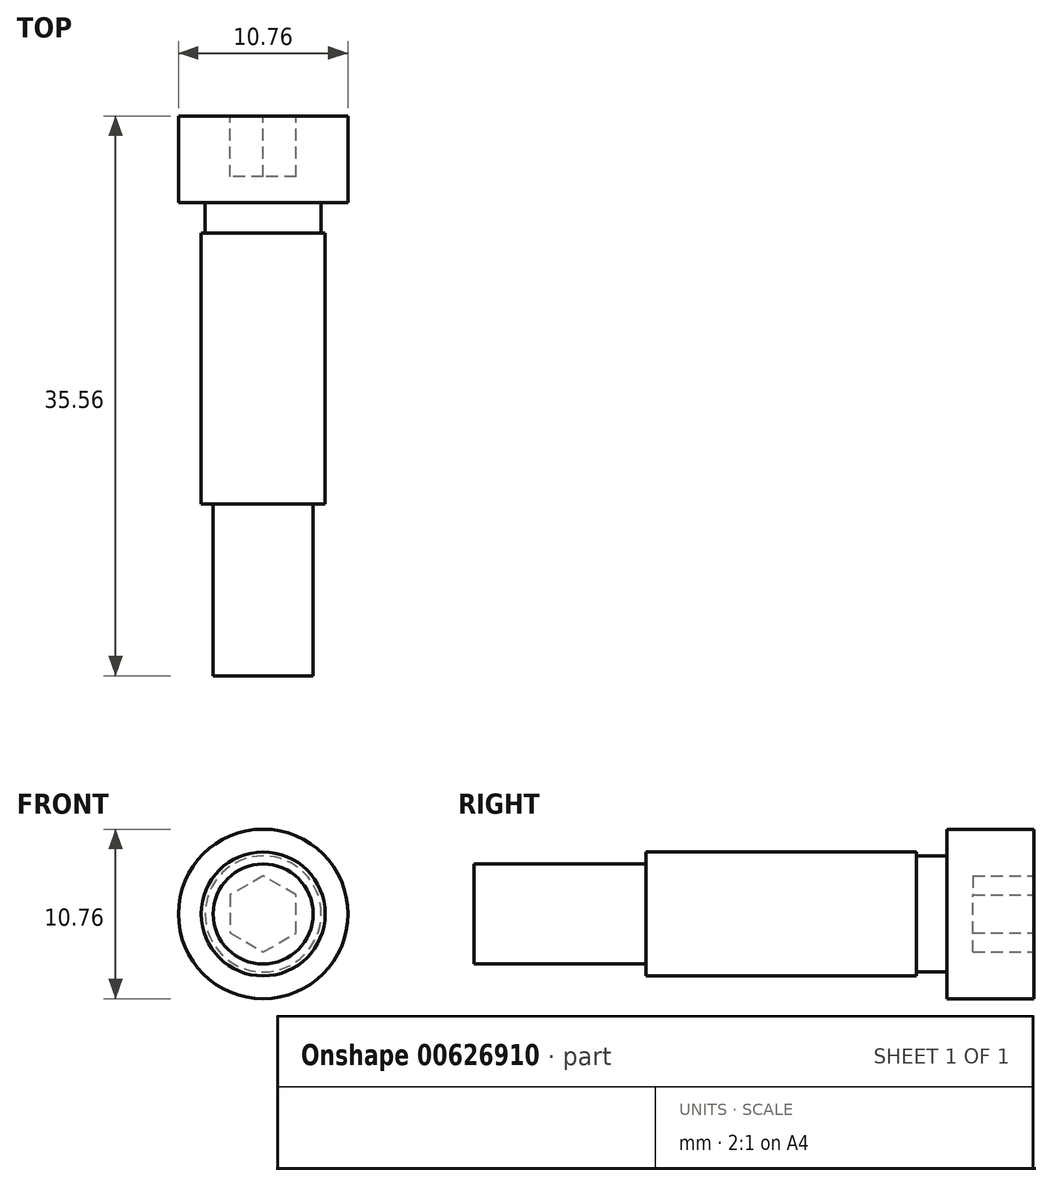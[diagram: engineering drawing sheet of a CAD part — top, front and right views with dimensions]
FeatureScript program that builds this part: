
annotation { "Feature Type Name" : "Feature", "Feature Type Description" : "" }
export const myFeature = defineFeature(function(context is Context, id is Id, definition is map)
    precondition{}
    {
        {
            var Q0;
            Q0=qCreatedBy(makeId("Right.planeOp"),FACE);
            var sketch = newSketch(context, id + "F0", { "sketchPlane" : qUnion([Q0])});
            skLineSegment(sketch, "E0", {"start": v(0, 0) * mm, "end": v(0, 3.17) * mm});
            skLineSegment(sketch, "E1", {"start": v(0, 3.18) * mm, "end": v(10.92, 3.18) * mm});
            skLineSegment(sketch, "E2", {"start": v(10.92, 3.18) * mm, "end": v(10.92, 3.94) * mm});
            skLineSegment(sketch, "E3", {"start": v(10.92, 3.94) * mm, "end": v(28.12, 3.94) * mm});
            skLineSegment(sketch, "E4", {"start": v(30.05, 3.94) * mm, "end": v(30.05, 5.38) * mm});
            skLineSegment(sketch, "E5", {"start": v(30.05, 5.38) * mm, "end": v(35.56, 5.38) * mm});
            skLineSegment(sketch, "E6", {"start": v(35.56, 5.38) * mm, "end": v(35.56, 0) * mm});
            skLineSegment(sketch, "E7", {"start": v(35.56, 0) * mm, "end": v(0, 0) * mm});
            skLineSegment(sketch, "E8", {"start": v(30.05, 3.94) * mm, "end": v(30.05, 3.68) * mm});
            skLineSegment(sketch, "E9", {"start": v(30.05, 3.68) * mm, "end": v(28.12, 3.68) * mm});
            skLineSegment(sketch, "E10", {"start": v(28.12, 3.68) * mm, "end": v(28.12, 3.94) * mm});
            skSolve(sketch);
        }
        {
            var Q0;
            Q0 = qSketchRegion(id + "F0", true);
            var Q1;
            Q1=sQuery(id+"F0.wireOp",EDGE,"E7");
            revolve(context, id + "F1", {"surfaceOperationType" : NewSurfaceOperationType.NEW, "entities" : qUnion([Q0]), "axis" : qUnion([Q1]), "revolveType" : RevolveType.FULL});
        }
        {
            var Q0;
            Q0=makeQuery(id+"F1.opRevolve","SWEPT_FACE",FACE,{"disambiguationData":[OSD([sQuery(id+"F0.wireOp",EDGE,"E6")])]});
            var sketch = newSketch(context, id + "F2", { "sketchPlane" : qUnion([Q0])});
            skCircle(sketch, "E11.cCircle", {"center": v(0, 0) * mm, "radius": 2.1 * mm, "construction": true});
            skLineSegment(sketch, "E11.0", {"start": v(0, 2.42) * mm, "end": v(2.1, 1.2) * mm});
            skLineSegment(sketch, "E11.1", {"start": v(2.1, 1.2) * mm, "end": v(2.1, -1.2) * mm});
            skLineSegment(sketch, "E11.2", {"start": v(2.1, -1.2) * mm, "end": v(0, -2.42) * mm});
            skLineSegment(sketch, "E11.3", {"start": v(0, -2.42) * mm, "end": v(-2.1, -1.2) * mm});
            skLineSegment(sketch, "E11.4", {"start": v(-2.1, -1.2) * mm, "end": v(-2.1, 1.2) * mm});
            skLineSegment(sketch, "E11.5", {"start": v(-2.1, 1.2) * mm, "end": v(0, 2.42) * mm});
            skPoint(sketch, "E11.0.midPoint", {"position": v(1.05, 1.81) * mm});
            skSolve(sketch);
        }
        {
            var Q0;
            Q0 = qSketchRegion(id + "F2", true);
            extrude(context, id + "F3", {"entities" : qUnion([Q0]), "operationType" : NewBodyOperationType.REMOVE, "oppositeDirection" : true, "depth" : 3.86 * mm, "offsetDistance" : 25.4 * mm});
        }
    });
